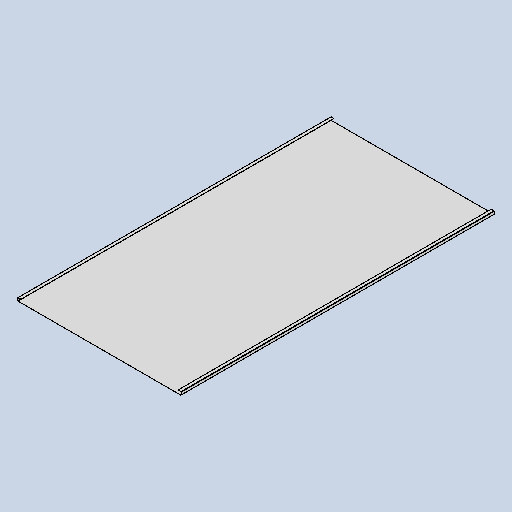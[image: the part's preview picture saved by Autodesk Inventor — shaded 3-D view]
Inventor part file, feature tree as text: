
AUTODESK INVENTOR PART (.ipt)
format: ipt  version: 2025 (Build 290162010, 162A)  size: 192,000 bytes
history: native  units: mm
features: sheet_metal_op x13, other x6, sketch x5, chamfer x1
ambient origin geometry x8: Origin, YZ Plane, XZ Plane, XY Plane, X Axis, Y Axis, Z Axis, Center Point
bodies: Body1 (feature_tree)
feature tree (25):
  sheet_metal_op  "Face1"
  sheet_metal_op  "Flange2"
  sheet_metal_op  "Flange3"
  sheet_metal_op  "Flange4"
  sheet_metal_op  "Flange5"
  chamfer  "Corner Round1"
  sketch  "Sketch6"  dims[d12=23.212879mm]
  other  "Plate2"
  sketch  "Sketch11"  dims[d52=511.8mm]
  other  "Plate4"
  sheet_metal_op  "Bend3"
  sheet_metal_op  "Corner3"
  sketch  "Sketch12"  dims[d53=980.0mm]
  other  "Plate5"
  sheet_metal_op  "Bend4"
  sheet_metal_op  "Corner4"
  sketch  "Sketch13"  dims[d54=0.5mm]
  other  "Plate6"
  sheet_metal_op  "Bend5"
  sheet_metal_op  "Corner5"
  sketch  "Sketch14"  dims[d84=0.5mm d85=0.25mm d86=1.0mm d87=0.5mm d88=10.0mm d89=90.0deg d90=0.5mm d91=2.0mm d92=0.5mm d93=0.5mm d94=0.5mm d95=0.25mm d96=1.0mm d97=0.5mm d98=10.0mm d99=90.0deg d100=0.5mm d101=2.0mm d102=0.5mm d103=0.5mm d104=0.5mm d105=0.25mm d106=1.0mm d107=0.5mm d108=10.0mm d109=90.0deg d110=0.5mm d111=2.0mm d112=0.5mm d113=0.5mm d114=0.5mm d115=0.25mm d116=1.0mm d117=0.5mm d118=10.0mm d119=90.0deg d120=0.5mm d121=2.0mm d122=0.5mm d123=0.5mm d124=4.0mm]
  other  "Plate7"
  sheet_metal_op  "Bend6"
  sheet_metal_op  "Corner6"
  other  "Definition1"
